# Revit family: 304_EVS_2_4 AB-_
name_source: partatom
category: Pipe Accessories
units: mm (PartAtom-declared; Revit-internal decimal feet)

## family parameters
Always vertical = Yes
Cut with Voids When Loaded = No
Part Type = Valve - Breaks Into
Round Connector Dimension = Use Diameter
Shared = No
Work Plane-Based = No

## types (3) — shared parameters
CAT0 = Yes
Description = EVS - Plug-in Insert for Temperature Control of Automatic Balancing Valve
L2D_Min = 3048 mm
L4 = 11 mm  [stored 0.0360892 ft]
L6 = 50 mm  [stored 0.164042 ft]
L6__ve = -50 mm  [stored -0.164042 ft]
L7 = 41 mm  [stored 0.134514 ft]
LA = 75 mm  [stored 0.246063 ft]
Manufacturer = FlowCon
QmdConnectorList = 301;D;302;D
R3 = 6 mm  [stored 0.019685 ft]
RA = 30 mm  [stored 0.0984252 ft]
URL = http://flowcon.com
magiPartTypeId = 304
magiProductFamilyId = EVS.2.4 AB-*
zero-valued in all types: MC_Default_elevation

## per-type parameters (varying)
| type | CenSd_RN_6 | CenSd_SW_6 | D | H11 | H12 | L1 | L1__ve | L2 | L2D | L3 | L3__ve | L5 | LL | R1 | R2 | RN | SW | W2D | magiProductId |
| EVS.2.01.B.4 | 9 mm | 12 mm  [stored 0.0393701 ft] | 15 mm | 24 mm | 56 mm | 16 mm  [stored 0.0524934 ft] | -16 mm | 49 mm | 82 mm | 64 mm | -64 mm | 32 mm | 41 mm  [stored 0.134514 ft] | 11 mm  [stored 0.0360892 ft] | 13 mm  [stored 0.0426509 ft] | 10 mm  [stored 0.0328084 ft] | 14 mm  [stored 0.0459318 ft] | 15 mm  [stored 0.0492126 ft] | EVS.2.4 AB-15 |
| EVS.2.09.B.4 | 11 mm  [stored 0.0360892 ft] | 16 mm  [stored 0.0524934 ft] | 25 mm | 23 mm | 54 mm | 20 mm  [stored 0.0656168 ft] | -20 mm | 61 mm | 102 mm | 62 mm | -62 mm | 31 mm  [stored 0.101706 ft] | 51 mm  [stored 0.167323 ft] | 14 mm  [stored 0.0459318 ft] | 16 mm  [stored 0.0524934 ft] | 13 mm  [stored 0.0426509 ft] | 18 mm  [stored 0.0590551 ft] | 25 mm  [stored 0.082021 ft] | EVS.2.4 AB-25 |
| EVS.2.02.B.4 | 10 mm  [stored 0.0328084 ft] | 14 mm  [stored 0.0459318 ft] | 20 mm | 23 mm | 55 mm | 19 mm | -19 mm | 56 mm | 94 mm | 63 mm | -63 mm | 32 mm | 47 mm  [stored 0.154199 ft] | 12 mm  [stored 0.0393701 ft] | 14 mm  [stored 0.0459318 ft] | 12 mm  [stored 0.0393701 ft] | 16 mm  [stored 0.0524934 ft] | 20 mm  [stored 0.0656168 ft] | EVS.2.4 AB-20 |

note: column(s) folded — value = type name in every type: magiProductCode

note: [stored X ft] marks values corroborated as IEEE doubles in the binary element streams (Revit-internal decimal feet)

## geometry (parser evidence)
native form markers: Sweep x2
no freeform markers — native parametric forms only
